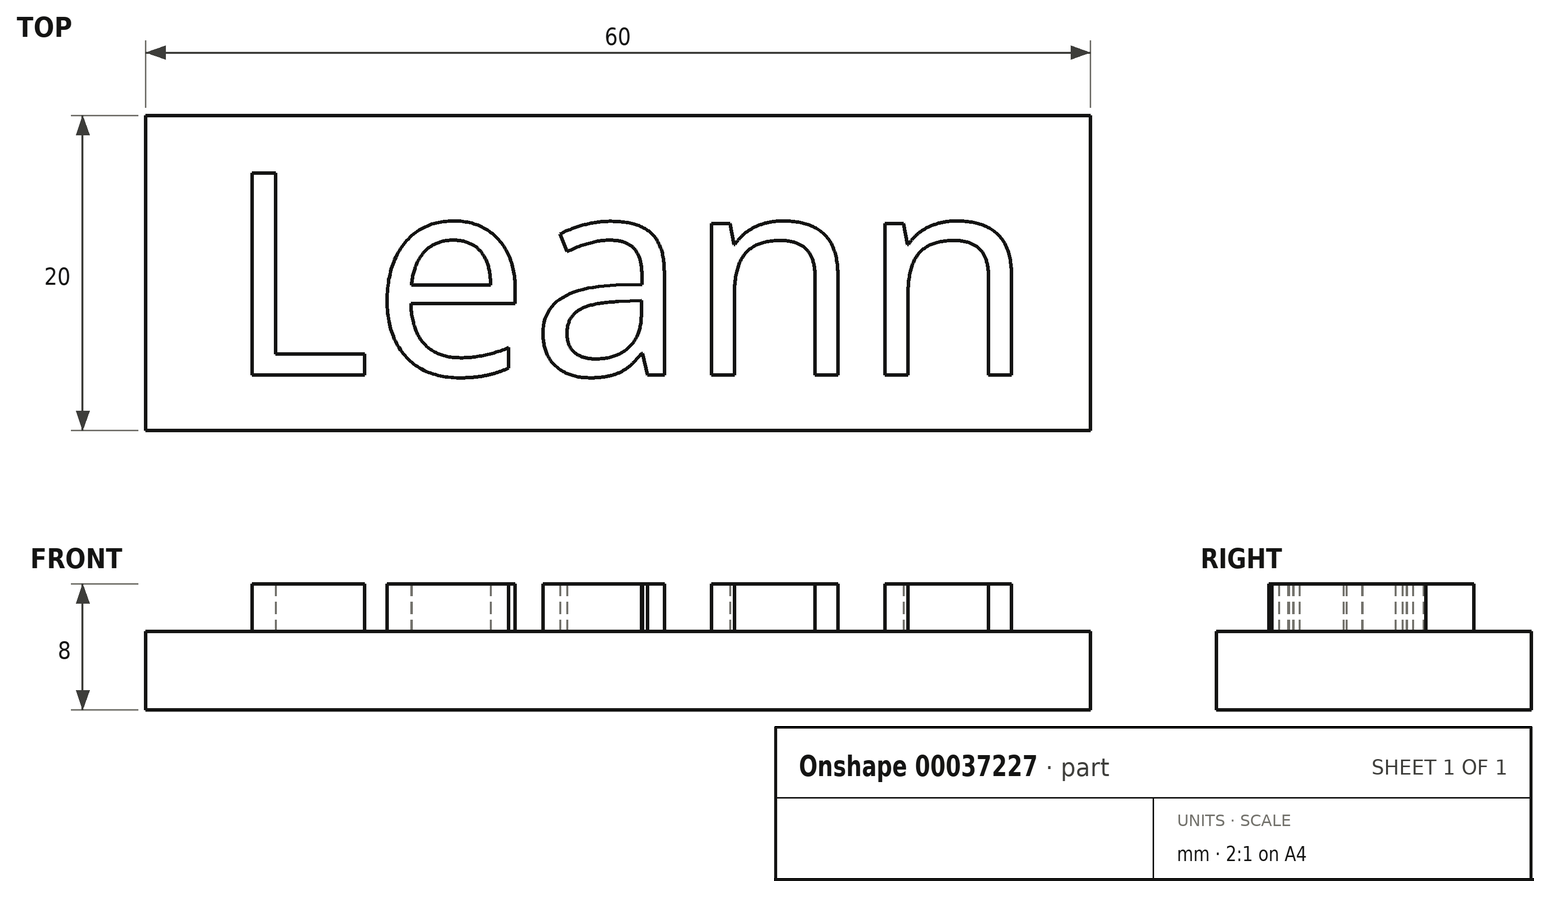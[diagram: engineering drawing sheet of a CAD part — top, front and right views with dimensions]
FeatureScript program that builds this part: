
annotation { "Feature Type Name" : "Feature", "Feature Type Description" : "" }
export const myFeature = defineFeature(function(context is Context, id is Id, definition is map)
    precondition{}
    {
        {
            var Q0;
            Q0=qCreatedBy(makeId("Top.planeOp"),FACE);
            var sketch = newSketch(context, id + "F0", { "sketchPlane" : qUnion([Q0])});
            skLineSegment(sketch, "E0.rect.bottom", {"start": v(30, 10) * mm, "end": v(-30, 10) * mm});
            skLineSegment(sketch, "E0.rect.top", {"start": v(30, -10) * mm, "end": v(-30, -10) * mm});
            skLineSegment(sketch, "E0.rect.left", {"start": v(30, 10) * mm, "end": v(30, -10) * mm});
            skLineSegment(sketch, "E0.rect.right", {"start": v(-30, 10) * mm, "end": v(-30, -10) * mm});
            skPoint(sketch, "E0.rect.middle", {"position": v(0, 0) * mm});
            skSolve(sketch);
        }
        {
            var Q0;
            Q0 = qSketchRegion(id + "F0", true);
            extrude(context, id + "F1", {"entities" : qUnion([Q0]), "depth" : 5 * mm});
        }
        {
            var Q0;
            Q0=makeQuery(id+"F1.opExtrude","CAP_FACE",FACE,{"disambiguationData":[OSD([sQuery(id+"F0.wireOp",EDGE,"E0.rect.bottom"),sQuery(id+"F0.wireOp",EDGE,"E0.rect.top"),sQuery(id+"F0.wireOp",EDGE,"E0.rect.left"),sQuery(id+"F0.wireOp",EDGE,"E0.rect.right")])],"isStart":false});
            var sketch = newSketch(context, id + "F2", { "sketchPlane" : qUnion([Q0])});
            skText(sketch, "E1", { "text": "Leann", "fontName": "OpenSans-Regular.ttf"});
            const initialGuessF2  = {"E1": [-0.025, -0.00648, 1, 0, 0.01293]};
            skSetInitialGuess(sketch, initialGuessF2);
            skSolve(sketch);
        }
        {
            var Q0;
            Q0 = qSketchRegion(id + "F2", true);
            extrude(context, id + "F3", {"entities" : qUnion([Q0]), "operationType" : NewBodyOperationType.ADD, "depth" : 3 * mm});
        }
    });
